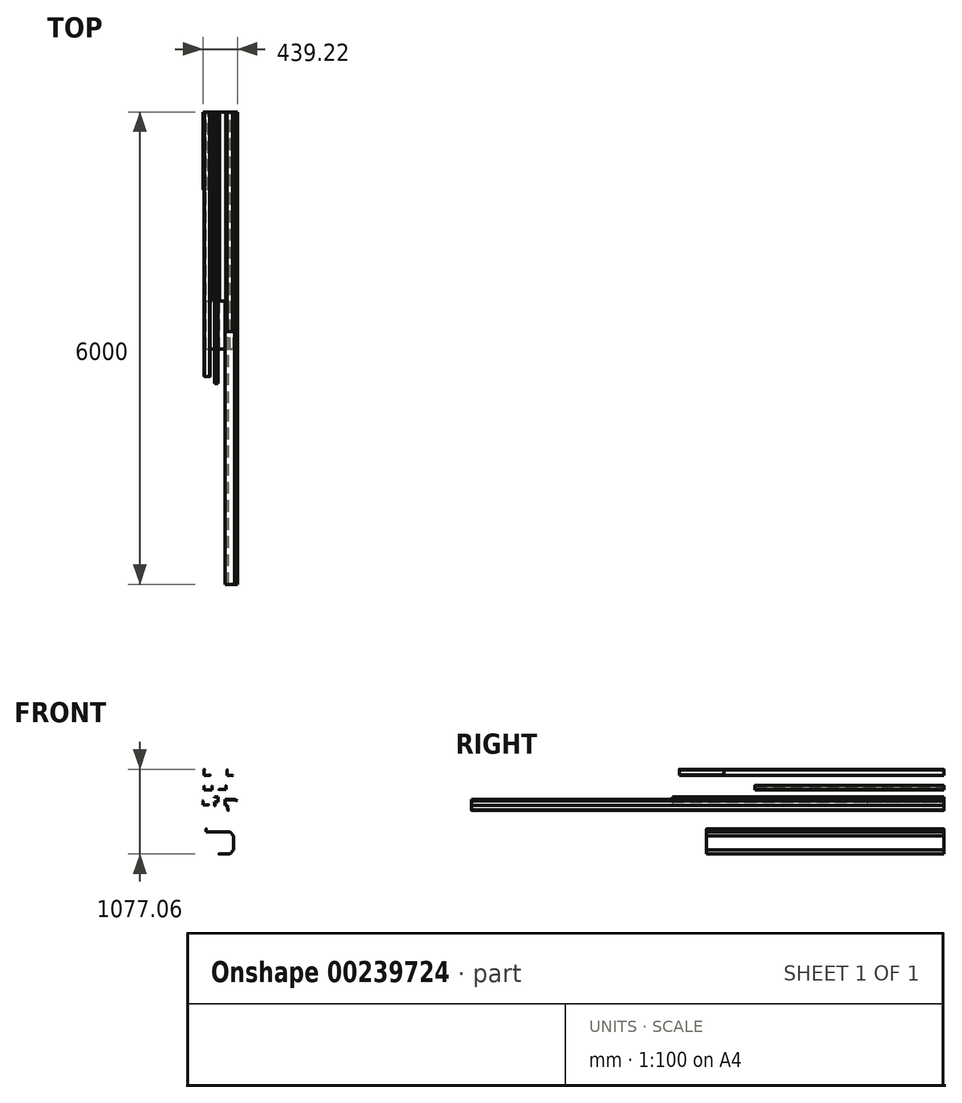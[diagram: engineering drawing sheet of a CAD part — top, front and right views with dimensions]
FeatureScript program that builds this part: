
annotation { "Feature Type Name" : "Feature", "Feature Type Description" : "" }
export const myFeature = defineFeature(function(context is Context, id is Id, definition is map)
    precondition{}
    {
        {
            var Q0;
            Q0=qCreatedBy(makeId("Front.planeOp"),FACE);
            var sketch = newSketch(context, id + "F0", { "sketchPlane" : qUnion([Q0])});
            skLineSegment(sketch, "E0", {"start": v(0, -0.5) * mm, "end": v(0, -75) * mm});
            skLineSegment(sketch, "E1", {"start": v(0, -75) * mm, "end": v(74.5, -75) * mm});
            skLineSegment(sketch, "E2", {"start": v(0.5, 0) * mm, "end": v(0.5, 0) * mm});
            skLineSegment(sketch, "E3", {"start": v(1, -0.5) * mm, "end": v(1, -10) * mm});
            skLineSegment(sketch, "E4", {"start": v(75, -74.5) * mm, "end": v(75, -74.5) * mm});
            skLineSegment(sketch, "E5", {"start": v(74.5, -74) * mm, "end": v(65, -74) * mm});
            skPoint(sketch, "E6.visualSharp", {"position": v(0, 0) * mm});
            skArc(sketch, "E6.filletArc", {"start": v(0.5, 0) * mm, "mid": v(0.15, -0.15) * mm, "end": v(0, -0.5) * mm});
            skPoint(sketch, "E7.visualSharp", {"position": v(1, 0) * mm});
            skArc(sketch, "E7.filletArc", {"start": v(1, -0.5) * mm, "mid": v(0.85, -0.15) * mm, "end": v(0.5, 0) * mm});
            skPoint(sketch, "E8.visualSharp", {"position": v(75, -74) * mm});
            skArc(sketch, "E8.filletArc", {"start": v(75, -74.5) * mm, "mid": v(74.85, -74.15) * mm, "end": v(74.5, -74) * mm});
            skPoint(sketch, "E9.visualSharp", {"position": v(75, -75) * mm});
            skArc(sketch, "E9.filletArc", {"start": v(74.5, -75) * mm, "mid": v(74.85, -74.85) * mm, "end": v(75, -74.5) * mm});
            skLineSegment(sketch, "E10.0", {"start": v(74.5, -73.5) * mm, "end": v(65, -73.5) * mm});
            skArc(sketch, "E10.1", {"start": v(75.5, -74.5) * mm, "mid": v(75.2, -73.8) * mm, "end": v(74.5, -73.5) * mm});
            skArc(sketch, "E10.2", {"start": v(74.5, -75.5) * mm, "mid": v(75.2, -75.2) * mm, "end": v(75.5, -74.5) * mm});
            skLineSegment(sketch, "E10.3", {"start": v(-0.5, -75.5) * mm, "end": v(74.5, -75.5) * mm});
            skLineSegment(sketch, "E10.4", {"start": v(1.5, -0.5) * mm, "end": v(1.5, -10) * mm});
            skArc(sketch, "E10.5", {"start": v(1.5, -0.5) * mm, "mid": v(1.2, 0.2) * mm, "end": v(0.5, 0.5) * mm});
            skArc(sketch, "E10.6", {"start": v(0.5, 0.5) * mm, "mid": v(-0.2, 0.2) * mm, "end": v(-0.5, -0.5) * mm});
            skLineSegment(sketch, "E10.7", {"start": v(-0.5, -0.5) * mm, "end": v(-0.5, -75.5) * mm});
            skLineSegment(sketch, "E11", {"start": v(65, -73.5) * mm, "end": v(65, -74) * mm});
            skLineSegment(sketch, "E12", {"start": v(1, -10) * mm, "end": v(1.5, -10) * mm});
            skSolve(sketch);
        }
        {
            var Q0;
            Q0 = qSketchRegion(id + "F0", true);
            extrude(context, id + "F1", {"entities" : qUnion([Q0]), "depth" : 3360 * mm});
        }
        {
            var Q0;
            Q0=qCreatedBy(makeId("Front.planeOp"),FACE);
            var sketch = newSketch(context, id + "F2", { "sketchPlane" : qUnion([Q0])});
            skLineSegment(sketch, "E13", {"start": v(291.67, -77.5) * mm, "end": v(291.67, -8) * mm});
            skLineSegment(sketch, "E14", {"start": v(291.67, -77.5) * mm, "end": v(361.17, -77.5) * mm});
            skLineSegment(sketch, "E15", {"start": v(263.67, -78) * mm, "end": v(263.67, -78) * mm});
            skLineSegment(sketch, "E16", {"start": v(361.17, -78.5) * mm, "end": v(351.67, -78.5) * mm});
            skLineSegment(sketch, "E17", {"start": v(193.17, -9.87) * mm, "end": v(193.17, -9.87) * mm});
            skLineSegment(sketch, "E18", {"start": v(290.67, -8) * mm, "end": v(290.67, -17.5) * mm});
            skPoint(sketch, "E19.visualSharp", {"position": v(290.67, -7.5) * mm});
            skArc(sketch, "E19.filletArc", {"start": v(291.17, -7.5) * mm, "mid": v(290.82, -7.64) * mm, "end": v(290.67, -8) * mm});
            skPoint(sketch, "E20.visualSharp", {"position": v(291.67, -7.5) * mm});
            skArc(sketch, "E20.filletArc", {"start": v(291.67, -8) * mm, "mid": v(291.52, -7.64) * mm, "end": v(291.17, -7.5) * mm});
            skPoint(sketch, "E21.visualSharp", {"position": v(361.67, -77.5) * mm});
            skArc(sketch, "E21.filletArc", {"start": v(361.67, -78) * mm, "mid": v(361.52, -77.64) * mm, "end": v(361.17, -77.5) * mm});
            skPoint(sketch, "E22.visualSharp", {"position": v(361.67, -78.5) * mm});
            skArc(sketch, "E22.filletArc", {"start": v(361.17, -78.5) * mm, "mid": v(361.52, -78.35) * mm, "end": v(361.67, -78) * mm});
            skLineSegment(sketch, "E23.0", {"start": v(290.17, -8) * mm, "end": v(290.17, -17.5) * mm});
            skArc(sketch, "E23.1", {"start": v(291.17, -7) * mm, "mid": v(290.46, -7.29) * mm, "end": v(290.17, -8) * mm});
            skArc(sketch, "E23.2", {"start": v(292.17, -8) * mm, "mid": v(291.88, -7.29) * mm, "end": v(291.17, -7) * mm});
            skLineSegment(sketch, "E23.3", {"start": v(292.17, -77) * mm, "end": v(292.17, -8) * mm});
            skLineSegment(sketch, "E23.4", {"start": v(361.17, -79) * mm, "end": v(351.67, -79) * mm});
            skArc(sketch, "E23.5", {"start": v(361.17, -79) * mm, "mid": v(361.88, -78.7) * mm, "end": v(362.17, -78) * mm});
            skArc(sketch, "E23.6", {"start": v(362.17, -78) * mm, "mid": v(361.88, -77.29) * mm, "end": v(361.17, -77) * mm});
            skLineSegment(sketch, "E23.7", {"start": v(292.17, -77) * mm, "end": v(361.17, -77) * mm});
            skLineSegment(sketch, "E24", {"start": v(290.17, -17.5) * mm, "end": v(290.67, -17.5) * mm});
            skLineSegment(sketch, "E25", {"start": v(351.67, -78.5) * mm, "end": v(351.67, -79) * mm});
            skSolve(sketch);
        }
        {
            var Q0;
            Q0 = qSketchRegion(id + "F2", true);
            extrude(context, id + "F3", {"entities" : qUnion([Q0]), "depth" : 2790 * mm});
        }
        {
            var Q0;
            Q0=qCreatedBy(makeId("Front.planeOp"),FACE);
            var sketch = newSketch(context, id + "F4", { "sketchPlane" : qUnion([Q0])});
            skLineSegment(sketch, "E26", {"start": v(0, -222.19) * mm, "end": v(0, -212.69) * mm});
            skLineSegment(sketch, "E27", {"start": v(-0.5, -212.19) * mm, "end": v(-0.5, -212.19) * mm});
            skLineSegment(sketch, "E28", {"start": v(-1, -212.69) * mm, "end": v(-1, -262.19) * mm});
            skLineSegment(sketch, "E29", {"start": v(-1, -262.19) * mm, "end": v(99, -262.19) * mm});
            skLineSegment(sketch, "E30", {"start": v(99, -262.19) * mm, "end": v(99, -212.69) * mm});
            skLineSegment(sketch, "E31", {"start": v(98.5, -212.19) * mm, "end": v(98.5, -212.19) * mm});
            skLineSegment(sketch, "E32", {"start": v(98, -212.69) * mm, "end": v(98, -222.19) * mm});
            skPoint(sketch, "E33.visualSharp", {"position": v(-1, -212.19) * mm});
            skArc(sketch, "E33.filletArc", {"start": v(-0.5, -212.19) * mm, "mid": v(-0.85, -212.33) * mm, "end": v(-1, -212.69) * mm});
            skPoint(sketch, "E34.visualSharp", {"position": v(0, -212.19) * mm});
            skArc(sketch, "E34.filletArc", {"start": v(0, -212.69) * mm, "mid": v(-0.15, -212.33) * mm, "end": v(-0.5, -212.19) * mm});
            skPoint(sketch, "E35.visualSharp", {"position": v(99, -212.19) * mm});
            skArc(sketch, "E35.filletArc", {"start": v(99, -212.69) * mm, "mid": v(98.85, -212.33) * mm, "end": v(98.5, -212.19) * mm});
            skPoint(sketch, "E36.visualSharp", {"position": v(98, -212.19) * mm});
            skArc(sketch, "E36.filletArc", {"start": v(98.5, -212.19) * mm, "mid": v(98.15, -212.33) * mm, "end": v(98, -212.69) * mm});
            skLineSegment(sketch, "E37.0", {"start": v(97.5, -212.69) * mm, "end": v(97.5, -222.19) * mm});
            skArc(sketch, "E37.1", {"start": v(98.5, -211.69) * mm, "mid": v(97.8, -211.98) * mm, "end": v(97.5, -212.69) * mm});
            skArc(sketch, "E37.2", {"start": v(99.5, -212.69) * mm, "mid": v(99.2, -211.98) * mm, "end": v(98.5, -211.69) * mm});
            skLineSegment(sketch, "E37.3", {"start": v(99.5, -262.69) * mm, "end": v(99.5, -212.69) * mm});
            skLineSegment(sketch, "E37.4", {"start": v(-1.5, -262.69) * mm, "end": v(99.5, -262.69) * mm});
            skLineSegment(sketch, "E37.5", {"start": v(0.5, -222.19) * mm, "end": v(0.5, -212.69) * mm});
            skArc(sketch, "E37.6", {"start": v(0.5, -212.69) * mm, "mid": v(0.2, -211.98) * mm, "end": v(-0.5, -211.69) * mm});
            skArc(sketch, "E37.7", {"start": v(-0.5, -211.69) * mm, "mid": v(-1.2, -211.98) * mm, "end": v(-1.5, -212.69) * mm});
            skLineSegment(sketch, "E37.8", {"start": v(-1.5, -212.69) * mm, "end": v(-1.5, -262.69) * mm});
            skLineSegment(sketch, "E38", {"start": v(0, -222.19) * mm, "end": v(0.5, -222.19) * mm});
            skLineSegment(sketch, "E39", {"start": v(98, -222.19) * mm, "end": v(97.5, -222.19) * mm});
            skSolve(sketch);
        }
        {
            var Q0;
            Q0 = qSketchRegion(id + "F4", true);
            extrude(context, id + "F5", {"entities" : qUnion([Q0]), "depth" : 2400 * mm});
        }
        {
            var Q0;
            Q0=qCreatedBy(makeId("Front.planeOp"),FACE);
            var sketch = newSketch(context, id + "F6", { "sketchPlane" : qUnion([Q0])});
            skLineSegment(sketch, "E40", {"start": v(195.63, -257) * mm, "end": v(186.13, -257) * mm});
            skLineSegment(sketch, "E41", {"start": v(185.63, -257.5) * mm, "end": v(185.63, -257.5) * mm});
            skLineSegment(sketch, "E42", {"start": v(186.13, -258) * mm, "end": v(275.63, -258) * mm});
            skLineSegment(sketch, "E43", {"start": v(275.63, -258) * mm, "end": v(275.63, -208.5) * mm});
            skLineSegment(sketch, "E44", {"start": v(275.13, -208) * mm, "end": v(275.13, -208) * mm});
            skLineSegment(sketch, "E45", {"start": v(274.63, -208.5) * mm, "end": v(274.63, -218) * mm});
            skPoint(sketch, "E46.visualSharp", {"position": v(274.63, -208) * mm});
            skArc(sketch, "E46.filletArc", {"start": v(275.13, -208) * mm, "mid": v(274.78, -208.14) * mm, "end": v(274.63, -208.5) * mm});
            skPoint(sketch, "E47.visualSharp", {"position": v(275.63, -208) * mm});
            skArc(sketch, "E47.filletArc", {"start": v(275.63, -208.5) * mm, "mid": v(275.48, -208.14) * mm, "end": v(275.13, -208) * mm});
            skPoint(sketch, "E48.visualSharp", {"position": v(185.63, -258) * mm});
            skArc(sketch, "E48.filletArc", {"start": v(185.63, -257.5) * mm, "mid": v(185.78, -257.85) * mm, "end": v(186.13, -258) * mm});
            skPoint(sketch, "E49.visualSharp", {"position": v(185.63, -257) * mm});
            skArc(sketch, "E49.filletArc", {"start": v(186.13, -257) * mm, "mid": v(185.78, -257.14) * mm, "end": v(185.63, -257.5) * mm});
            skLineSegment(sketch, "E50.0", {"start": v(274.13, -208.5) * mm, "end": v(274.13, -218) * mm});
            skArc(sketch, "E50.1", {"start": v(275.13, -207.5) * mm, "mid": v(274.42, -207.79) * mm, "end": v(274.13, -208.5) * mm});
            skArc(sketch, "E50.2", {"start": v(276.13, -208.5) * mm, "mid": v(275.84, -207.79) * mm, "end": v(275.13, -207.5) * mm});
            skLineSegment(sketch, "E50.3", {"start": v(276.13, -258.5) * mm, "end": v(276.13, -208.5) * mm});
            skLineSegment(sketch, "E50.4", {"start": v(195.63, -256.5) * mm, "end": v(186.13, -256.5) * mm});
            skArc(sketch, "E50.5", {"start": v(186.13, -256.5) * mm, "mid": v(185.42, -256.79) * mm, "end": v(185.13, -257.5) * mm});
            skArc(sketch, "E50.6", {"start": v(185.13, -257.5) * mm, "mid": v(185.42, -258.2) * mm, "end": v(186.13, -258.5) * mm});
            skLineSegment(sketch, "E50.7", {"start": v(186.13, -258.5) * mm, "end": v(276.13, -258.5) * mm});
            skLineSegment(sketch, "E51", {"start": v(195.63, -256.5) * mm, "end": v(195.63, -257) * mm});
            skLineSegment(sketch, "E52", {"start": v(274.63, -218) * mm, "end": v(274.13, -218) * mm});
            skSolve(sketch);
        }
        {
            var Q0;
            Q0 = qSketchRegion(id + "F6", true);
            extrude(context, id + "F7", {"entities" : qUnion([Q0]), "depth" : 2400 * mm});
        }
        {
            var Q0;
            Q0=qCreatedBy(makeId("Front.planeOp"),FACE);
            var sketch = newSketch(context, id + "F8", { "sketchPlane" : qUnion([Q0])});
            skLineSegment(sketch, "E53", {"start": v(-18, -402.68) * mm, "end": v(-18, -452.18) * mm});
            skLineSegment(sketch, "E54", {"start": v(-18, -452.18) * mm, "end": v(56.5, -452.18) * mm});
            skLineSegment(sketch, "E55", {"start": v(75, -451.68) * mm, "end": v(75, -451.68) * mm});
            skLineSegment(sketch, "E56", {"start": v(56.5, -451.18) * mm, "end": v(47, -451.18) * mm});
            skLineSegment(sketch, "E57", {"start": v(0.5, -402.18) * mm, "end": v(0.5, -402.18) * mm});
            skLineSegment(sketch, "E58", {"start": v(-17, -402.68) * mm, "end": v(-17, -412.18) * mm});
            skPoint(sketch, "E59.visualSharp", {"position": v(-18, -402.18) * mm});
            skArc(sketch, "E59.filletArc", {"start": v(-17.5, -402.18) * mm, "mid": v(-17.85, -402.33) * mm, "end": v(-18, -402.68) * mm});
            skPoint(sketch, "E60.visualSharp", {"position": v(-17, -402.18) * mm});
            skArc(sketch, "E60.filletArc", {"start": v(-17, -402.68) * mm, "mid": v(-17.15, -402.33) * mm, "end": v(-17.5, -402.18) * mm});
            skPoint(sketch, "E61.visualSharp", {"position": v(57, -452.18) * mm});
            skArc(sketch, "E61.filletArc", {"start": v(56.5, -452.18) * mm, "mid": v(56.85, -452.04) * mm, "end": v(57, -451.68) * mm});
            skPoint(sketch, "E62.visualSharp", {"position": v(57, -451.18) * mm});
            skArc(sketch, "E62.filletArc", {"start": v(57, -451.68) * mm, "mid": v(56.85, -451.33) * mm, "end": v(56.5, -451.18) * mm});
            skLineSegment(sketch, "E63.0", {"start": v(56.5, -450.68) * mm, "end": v(47, -450.68) * mm});
            skArc(sketch, "E63.1", {"start": v(57.5, -451.68) * mm, "mid": v(57.2, -450.98) * mm, "end": v(56.5, -450.68) * mm});
            skArc(sketch, "E63.2", {"start": v(56.5, -452.68) * mm, "mid": v(57.2, -452.39) * mm, "end": v(57.5, -451.68) * mm});
            skLineSegment(sketch, "E63.3", {"start": v(-18.5, -452.68) * mm, "end": v(56.5, -452.68) * mm});
            skLineSegment(sketch, "E63.4", {"start": v(-16.5, -402.68) * mm, "end": v(-16.5, -412.18) * mm});
            skArc(sketch, "E63.5", {"start": v(-16.5, -402.68) * mm, "mid": v(-16.8, -401.98) * mm, "end": v(-17.5, -401.68) * mm});
            skArc(sketch, "E63.6", {"start": v(-17.5, -401.68) * mm, "mid": v(-18.2, -401.98) * mm, "end": v(-18.5, -402.68) * mm});
            skLineSegment(sketch, "E63.7", {"start": v(-18.5, -402.68) * mm, "end": v(-18.5, -452.68) * mm});
            skLineSegment(sketch, "E64", {"start": v(47, -450.68) * mm, "end": v(47, -451.18) * mm});
            skLineSegment(sketch, "E65", {"start": v(-16.5, -412.18) * mm, "end": v(-17, -412.18) * mm});
            skSolve(sketch);
        }
        {
            var Q0;
            Q0 = qSketchRegion(id + "F8", true);
            extrude(context, id + "F9", {"entities" : qUnion([Q0]), "depth" : 980 * mm});
        }
        {
            var Q0;
            Q0=qCreatedBy(makeId("Front.planeOp"),FACE);
            var sketch = newSketch(context, id + "F10", { "sketchPlane" : qUnion([Q0])});
            skLineSegment(sketch, "E66", {"start": v(133.68, -353.43) * mm, "end": v(173.68, -353.43) * mm});
            skLineSegment(sketch, "E67", {"start": v(173.68, -353.43) * mm, "end": v(173.68, -413.43) * mm});
            skLineSegment(sketch, "E68", {"start": v(173.68, -413.43) * mm, "end": v(133.68, -413.43) * mm});
            skLineSegment(sketch, "E69", {"start": v(133.68, -413.43) * mm, "end": v(133.68, -462.93) * mm});
            skLineSegment(sketch, "E70", {"start": v(133.18, -463.43) * mm, "end": v(133.18, -463.43) * mm});
            skLineSegment(sketch, "E71", {"start": v(132.68, -462.93) * mm, "end": v(132.68, -453.43) * mm});
            skLineSegment(sketch, "E72", {"start": v(133.68, -353.43) * mm, "end": v(128.68, -362.1) * mm});
            skPoint(sketch, "E73.visualSharp", {"position": v(132.68, -463.43) * mm});
            skArc(sketch, "E73.filletArc", {"start": v(132.68, -462.93) * mm, "mid": v(132.83, -463.28) * mm, "end": v(133.18, -463.43) * mm});
            skPoint(sketch, "E74.visualSharp", {"position": v(133.68, -463.43) * mm});
            skArc(sketch, "E74.filletArc", {"start": v(133.18, -463.43) * mm, "mid": v(133.54, -463.28) * mm, "end": v(133.68, -462.93) * mm});
            skLineSegment(sketch, "E75.0", {"start": v(132.18, -462.93) * mm, "end": v(132.18, -453.43) * mm});
            skArc(sketch, "E75.1", {"start": v(132.18, -462.93) * mm, "mid": v(132.48, -463.64) * mm, "end": v(133.18, -463.93) * mm});
            skArc(sketch, "E75.2", {"start": v(133.18, -463.93) * mm, "mid": v(133.89, -463.64) * mm, "end": v(134.18, -462.93) * mm});
            skLineSegment(sketch, "E75.3", {"start": v(134.18, -413.93) * mm, "end": v(134.18, -462.93) * mm});
            skLineSegment(sketch, "E75.4", {"start": v(133.4, -352.93) * mm, "end": v(128.25, -361.84) * mm});
            skLineSegment(sketch, "E75.5", {"start": v(133.4, -352.93) * mm, "end": v(174.18, -352.93) * mm});
            skLineSegment(sketch, "E75.6", {"start": v(174.18, -352.93) * mm, "end": v(174.18, -413.93) * mm});
            skLineSegment(sketch, "E75.7", {"start": v(174.18, -413.93) * mm, "end": v(134.18, -413.93) * mm});
            skLineSegment(sketch, "E76", {"start": v(128.25, -361.84) * mm, "end": v(128.68, -362.1) * mm});
            skLineSegment(sketch, "E77", {"start": v(132.18, -453.43) * mm, "end": v(132.68, -453.43) * mm});
            skSolve(sketch);
        }
        {
            var Q0;
            Q0 = qSketchRegion(id + "F10", true);
            extrude(context, id + "F11", {"entities" : qUnion([Q0]), "depth" : 3450 * mm});
        }
        {
            var Q0;
            Q0=qCreatedBy(makeId("Front.planeOp"),FACE);
            var sketch = newSketch(context, id + "F12", { "sketchPlane" : qUnion([Q0])});
            skLineSegment(sketch, "E78", {"start": v(382.96, -386.15) * mm, "end": v(262.96, -386.15) * mm});
            skLineSegment(sketch, "E79", {"start": v(262.96, -386.15) * mm, "end": v(262.96, -456.15) * mm});
            skLineSegment(sketch, "E80", {"start": v(262.96, -456.15) * mm, "end": v(292.96, -456.15) * mm});
            skLineSegment(sketch, "E81", {"start": v(292.96, -456.15) * mm, "end": v(305.03, -524.6) * mm});
            skLineSegment(sketch, "E82", {"start": v(305.6, -525) * mm, "end": v(305.6, -525) * mm});
            skLineSegment(sketch, "E83", {"start": v(306.02, -524.42) * mm, "end": v(304.37, -515.07) * mm});
            skLineSegment(sketch, "E84", {"start": v(382.96, -386.15) * mm, "end": v(420.55, -399.83) * mm});
            skPoint(sketch, "E85.visualSharp", {"position": v(305.12, -525.09) * mm});
            skArc(sketch, "E85.filletArc", {"start": v(305.03, -524.6) * mm, "mid": v(305.24, -524.92) * mm, "end": v(305.6, -525) * mm});
            skPoint(sketch, "E86.visualSharp", {"position": v(306.1, -524.92) * mm});
            skArc(sketch, "E86.filletArc", {"start": v(305.6, -525) * mm, "mid": v(305.93, -524.8) * mm, "end": v(306.02, -524.42) * mm});
            skLineSegment(sketch, "E87.0", {"start": v(306.5, -524.34) * mm, "end": v(304.86, -514.98) * mm});
            skArc(sketch, "E87.1", {"start": v(305.7, -525.5) * mm, "mid": v(306.34, -525.08) * mm, "end": v(306.5, -524.34) * mm});
            skArc(sketch, "E87.2", {"start": v(304.54, -524.68) * mm, "mid": v(304.95, -525.33) * mm, "end": v(305.7, -525.5) * mm});
            skLineSegment(sketch, "E87.3", {"start": v(292.54, -456.65) * mm, "end": v(304.54, -524.68) * mm});
            skLineSegment(sketch, "E87.4", {"start": v(383.05, -385.65) * mm, "end": v(420.72, -399.36) * mm});
            skLineSegment(sketch, "E87.5", {"start": v(383.05, -385.65) * mm, "end": v(262.46, -385.65) * mm});
            skLineSegment(sketch, "E87.6", {"start": v(262.46, -385.65) * mm, "end": v(262.46, -456.65) * mm});
            skLineSegment(sketch, "E87.7", {"start": v(262.46, -456.65) * mm, "end": v(292.54, -456.65) * mm});
            skLineSegment(sketch, "E88", {"start": v(304.86, -514.98) * mm, "end": v(304.37, -515.07) * mm});
            skLineSegment(sketch, "E89", {"start": v(420.72, -399.36) * mm, "end": v(420.55, -399.83) * mm});
            skSolve(sketch);
        }
        {
            var Q0;
            Q0 = qSketchRegion(id + "F12", true);
            extrude(context, id + "F13", {"entities" : qUnion([Q0]), "depth" : 6000 * mm});
        }
        {
            var Q0;
            Q0=qCreatedBy(makeId("Front.planeOp"),FACE);
            var sketch = newSketch(context, id + "F14", { "sketchPlane" : qUnion([Q0])});
            skLineSegment(sketch, "E90", {"start": v(25.36, -757.52) * mm, "end": v(25.36, -797.02) * mm});
            skLineSegment(sketch, "E91", {"start": v(25.36, -797.02) * mm, "end": v(325.36, -797.02) * mm});
            skLineSegment(sketch, "E92", {"start": v(325.36, -797.02) * mm, "end": v(372.2, -849.04) * mm});
            skLineSegment(sketch, "E93", {"start": v(372.2, -849.04) * mm, "end": v(372.2, -1024.04) * mm});
            skLineSegment(sketch, "E94", {"start": v(372.2, -1024.04) * mm, "end": v(325.36, -1076.06) * mm});
            skLineSegment(sketch, "E95", {"start": v(325.36, -1076.06) * mm, "end": v(185.86, -1076.06) * mm});
            skLineSegment(sketch, "E96", {"start": v(185.36, -1075.56) * mm, "end": v(185.36, -1075.56) * mm});
            skLineSegment(sketch, "E97", {"start": v(185.86, -1075.06) * mm, "end": v(195.36, -1075.06) * mm});
            skPoint(sketch, "E98.visualSharp", {"position": v(185.36, -1076.06) * mm});
            skArc(sketch, "E98.filletArc", {"start": v(185.36, -1075.56) * mm, "mid": v(185.5, -1075.92) * mm, "end": v(185.86, -1076.06) * mm});
            skPoint(sketch, "E99.visualSharp", {"position": v(185.36, -1075.06) * mm});
            skArc(sketch, "E99.filletArc", {"start": v(185.86, -1075.06) * mm, "mid": v(185.5, -1075.2) * mm, "end": v(185.36, -1075.56) * mm});
            skLineSegment(sketch, "E100.0", {"start": v(185.86, -1074.56) * mm, "end": v(195.36, -1074.56) * mm});
            skLineSegment(sketch, "E100.1", {"start": v(185.86, -1074.56) * mm, "end": v(185.86, -1074.56) * mm});
            skArc(sketch, "E100.2", {"start": v(185.86, -1074.56) * mm, "mid": v(184.86, -1075.56) * mm, "end": v(185.86, -1076.56) * mm});
            skLineSegment(sketch, "E100.3", {"start": v(325.58, -1076.56) * mm, "end": v(185.86, -1076.56) * mm});
            skLineSegment(sketch, "E100.4", {"start": v(372.7, -1024.23) * mm, "end": v(325.58, -1076.56) * mm});
            skLineSegment(sketch, "E100.5", {"start": v(25.86, -757.52) * mm, "end": v(25.86, -796.52) * mm});
            skLineSegment(sketch, "E100.6", {"start": v(25.86, -796.52) * mm, "end": v(325.58, -796.52) * mm});
            skLineSegment(sketch, "E100.7", {"start": v(325.58, -796.52) * mm, "end": v(372.7, -848.85) * mm});
            skLineSegment(sketch, "E100.8", {"start": v(372.7, -848.85) * mm, "end": v(372.7, -1024.23) * mm});
            skLineSegment(sketch, "E101", {"start": v(24.86, -757.02) * mm, "end": v(24.86, -757.02) * mm});
            skLineSegment(sketch, "E102", {"start": v(24.36, -757.52) * mm, "end": v(24.36, -767.02) * mm});
            skPoint(sketch, "E103.visualSharp", {"position": v(25.36, -757.02) * mm});
            skArc(sketch, "E103.filletArc", {"start": v(25.36, -757.52) * mm, "mid": v(25.21, -757.17) * mm, "end": v(24.86, -757.02) * mm});
            skPoint(sketch, "E104.visualSharp", {"position": v(24.36, -757.02) * mm});
            skArc(sketch, "E104.filletArc", {"start": v(24.86, -757.02) * mm, "mid": v(24.5, -757.17) * mm, "end": v(24.36, -757.52) * mm});
            skLineSegment(sketch, "E105.0", {"start": v(23.86, -757.52) * mm, "end": v(23.86, -767.02) * mm});
            skArc(sketch, "E105.1", {"start": v(24.86, -756.52) * mm, "mid": v(24.15, -756.82) * mm, "end": v(23.86, -757.52) * mm});
            skArc(sketch, "E105.2", {"start": v(25.86, -757.52) * mm, "mid": v(25.56, -756.82) * mm, "end": v(24.86, -756.52) * mm});
            skLineSegment(sketch, "E106", {"start": v(23.86, -767.02) * mm, "end": v(24.36, -767.02) * mm});
            skLineSegment(sketch, "E107", {"start": v(195.36, -1075.06) * mm, "end": v(195.36, -1074.56) * mm});
            skSolve(sketch);
        }
        {
            var Q0;
            Q0 = qSketchRegion(id + "F14", true);
            extrude(context, id + "F15", {"entities" : qUnion([Q0]), "depth" : 3015 * mm});
        }
    });
